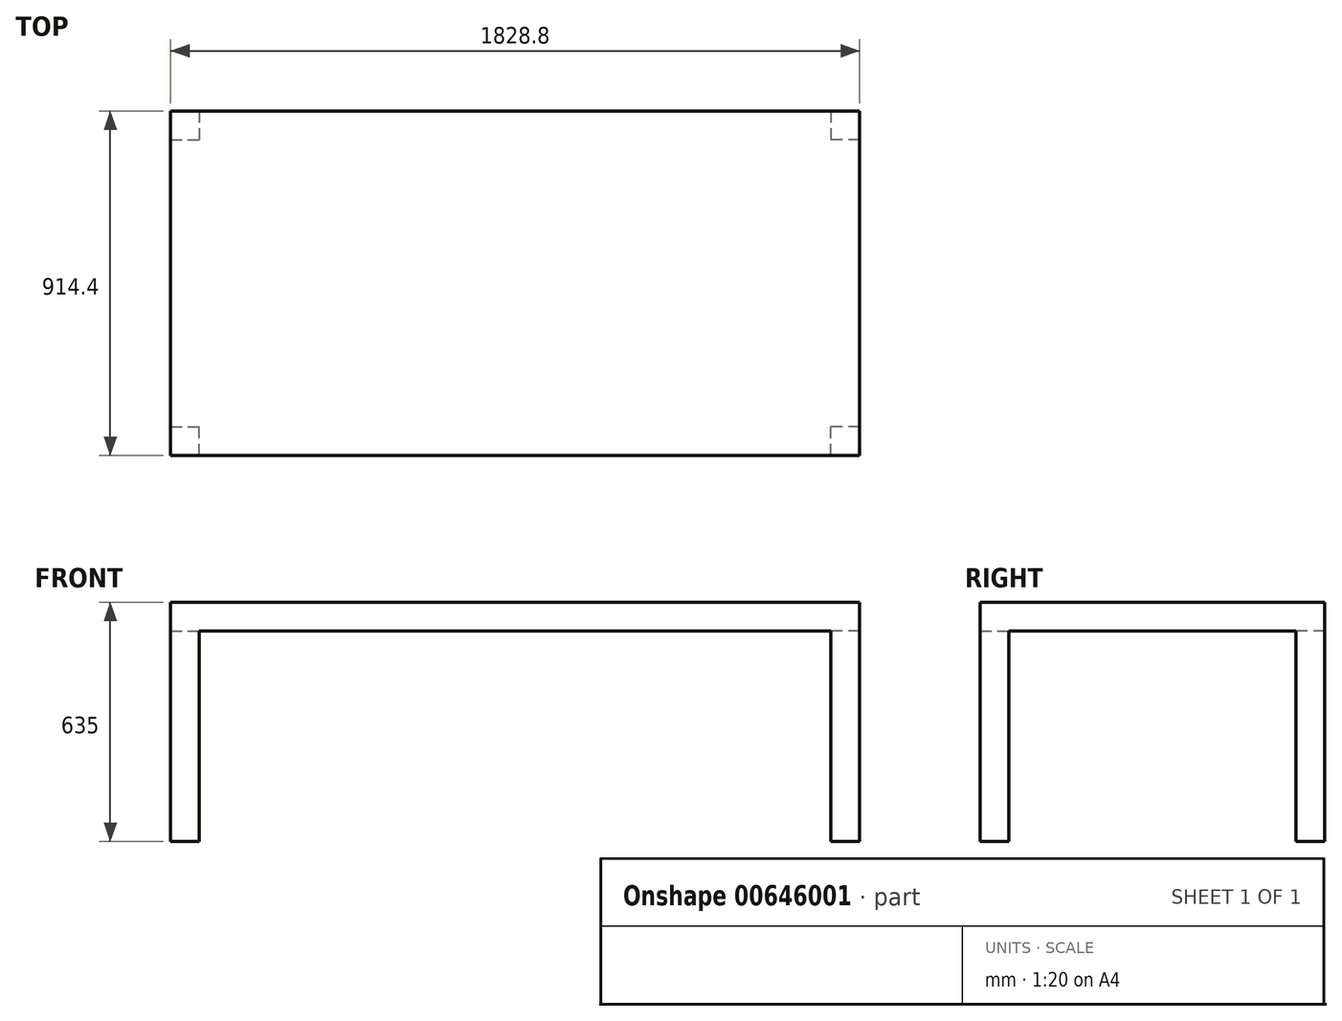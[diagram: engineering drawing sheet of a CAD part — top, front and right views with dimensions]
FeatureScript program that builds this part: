
annotation { "Feature Type Name" : "Feature", "Feature Type Description" : "" }
export const myFeature = defineFeature(function(context is Context, id is Id, definition is map)
    precondition{}
    {
        {
            var Q0;
            Q0=qCreatedBy(makeId("Top.planeOp"),FACE);
            var sketch = newSketch(context, id + "F0", { "sketchPlane" : qUnion([Q0])});
            skLineSegment(sketch, "E0.bottom", {"start": v(914.4, 457.2) * mm, "end": v(-914.4, 457.2) * mm});
            skLineSegment(sketch, "E0.top", {"start": v(914.4, -457.2) * mm, "end": v(-914.4, -457.2) * mm});
            skLineSegment(sketch, "E0.left", {"start": v(914.4, 457.2) * mm, "end": v(914.4, -457.2) * mm});
            skLineSegment(sketch, "E0.right", {"start": v(-914.4, 457.2) * mm, "end": v(-914.4, -457.2) * mm});
            skPoint(sketch, "E0.middle", {"position": v(0, 0) * mm});
            skSolve(sketch);
        }
        {
            var Q0;
            Q0=makeQuery(id+"F0.imprint","IMPRINT",FACE,{"disambiguationData":[TD([[makeQuery(id+"F0.imprint","IMPRINT",EDGE,{"derivedFrom":sQuery(id+"F0.wireOp",EDGE,"E0.bottom")}),1.0]])]});
            extrude(context, id + "F1", {"entities" : qUnion([Q0]), "depth" : 635 * mm, "offsetDistance" : 25.4 * mm});
        }
        {
            var Q0;
            Q0=makeQuery(id+"F1.opExtrude","CAP_FACE",FACE,{"disambiguationData":[OSD([sQuery(id+"F0.wireOp",EDGE,"E0.bottom"),sQuery(id+"F0.wireOp",EDGE,"E0.top"),sQuery(id+"F0.wireOp",EDGE,"E0.left"),sQuery(id+"F0.wireOp",EDGE,"E0.right")])],"isStart":true});
            var sketch = newSketch(context, id + "F2", { "sketchPlane" : qUnion([Q0])});
            skLineSegment(sketch, "E1.bottom", {"start": v(-914.4, 457.2) * mm, "end": v(-838.2, 457.2) * mm});
            skLineSegment(sketch, "E1.top", {"start": v(-914.4, 381) * mm, "end": v(-838.2, 381) * mm});
            skLineSegment(sketch, "E1.left", {"start": v(-914.4, 457.2) * mm, "end": v(-914.4, 381) * mm});
            skLineSegment(sketch, "E1.right", {"start": v(-838.2, 457.2) * mm, "end": v(-838.2, 381) * mm});
            skLineSegment(sketch, "E2.bottom", {"start": v(-914.4, -457.2) * mm, "end": v(-838.2, -457.2) * mm});
            skLineSegment(sketch, "E2.top", {"start": v(-914.4, -381) * mm, "end": v(-838.2, -381) * mm});
            skLineSegment(sketch, "E2.left", {"start": v(-914.4, -457.2) * mm, "end": v(-914.4, -381) * mm});
            skLineSegment(sketch, "E2.right", {"start": v(-838.2, -457.2) * mm, "end": v(-838.2, -381) * mm});
            skPoint(sketch, "E3.oppositeSnap0", {"position": v(-876.3, -381) * mm});
            skLineSegment(sketch, "E3.bottom", {"start": v(914.4, -457.2) * mm, "end": v(838.2, -457.2) * mm});
            skLineSegment(sketch, "E3.top", {"start": v(914.4, -381) * mm, "end": v(838.2, -381) * mm});
            skLineSegment(sketch, "E3.left", {"start": v(914.4, -457.2) * mm, "end": v(914.4, -381) * mm});
            skLineSegment(sketch, "E3.right", {"start": v(838.2, -457.2) * mm, "end": v(838.2, -381) * mm});
            skLineSegment(sketch, "E4.bottom", {"start": v(914.4, 457.2) * mm, "end": v(838.2, 457.2) * mm});
            skLineSegment(sketch, "E4.top", {"start": v(914.4, 381) * mm, "end": v(838.2, 381) * mm});
            skLineSegment(sketch, "E4.left", {"start": v(914.4, 457.2) * mm, "end": v(914.4, 381) * mm});
            skLineSegment(sketch, "E4.right", {"start": v(838.2, 457.2) * mm, "end": v(838.2, 381) * mm});
            skSolve(sketch);
        }
        {
            var Q0;
            {var subQ6=sQuery(id+"F2.wireOp",EDGE,"E1.top");Q0=makeQuery(id+"F2.imprint","IMPRINT",FACE,{"disambiguationData":[TD([[makeQuery(id+"F2.imprint","IMPRINT",EDGE,{"derivedFrom":subQ6}),-1.0]])]});}
            extrude(context, id + "F3", {"entities" : qUnion([Q0]), "operationType" : NewBodyOperationType.REMOVE, "oppositeDirection" : true, "depth" : 558.8 * mm, "offsetDistance" : 25.4 * mm});
        }
    });
